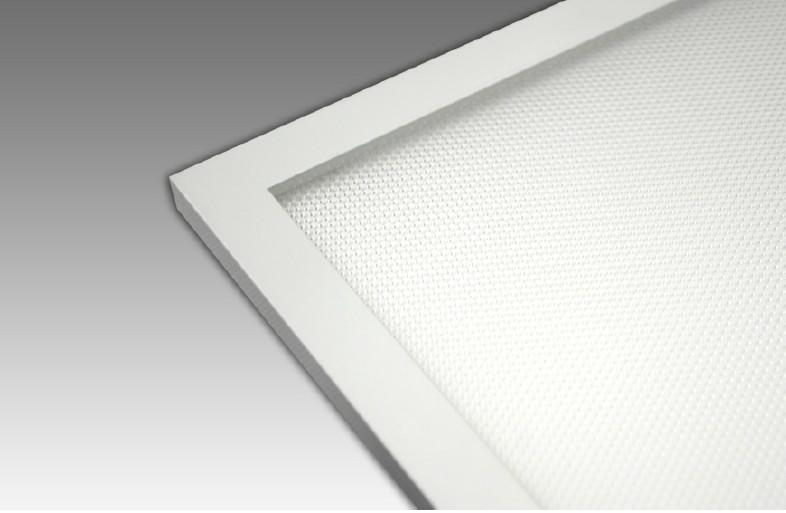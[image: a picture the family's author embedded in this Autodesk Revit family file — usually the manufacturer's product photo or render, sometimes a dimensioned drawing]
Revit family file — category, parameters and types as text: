
# Revit family: DG1012MOW
name_source: partatom
category: Lighting Fixtures
revit_build: Autodesk Revit 2017 (Build: 20160225_1515(x64)
units: mm (PartAtom-declared; Revit-internal decimal feet)

## family parameters
Cut with Voids When Loaded = No
Host = Face
Light Source = Yes
Part Type = Normal
Room Calculation Point = No
Round Connector Dimension = Use Diameter
Shared = No

## types (4) — shared parameters
Color Filter = 16777215
Default Elevation = 1219 mm
Dimming Lamp Color Temperature Shift = <None>
Emit Shape Visible in Rendering = Yes
Emit from Circle Diameter = 79 mm
Lamp = LED
Manufacturer = ARLIGHT
Model = DG1012MON
Tilt Angle = 90.00°
Type Comments = DOWNLIGHT
Type Image = <None>

## per-type parameters (varying)
| type | Apparent Load | Photometric Web File | Wattage Comments |
| DGMOW.120.7.30 | 7 VA | dg-1012-mow-7w-3k-sg.ies | 7 |
| DGMOW.120.7.40 | 7 VA | dg-1012-mow-7w-4k-sg.ies | 7 |
| DGMOW.120.10.30 | 10 VA | dg-1012-mow-10w-3k-sg.ies | 10 |
| DGMOW.120.10.40 | 10 VA | dg-1012-mow-10w-4k-sg.ies | 10 |

## geometry (parser evidence)
native form markers: Sweep x3
no freeform markers — native parametric forms only
